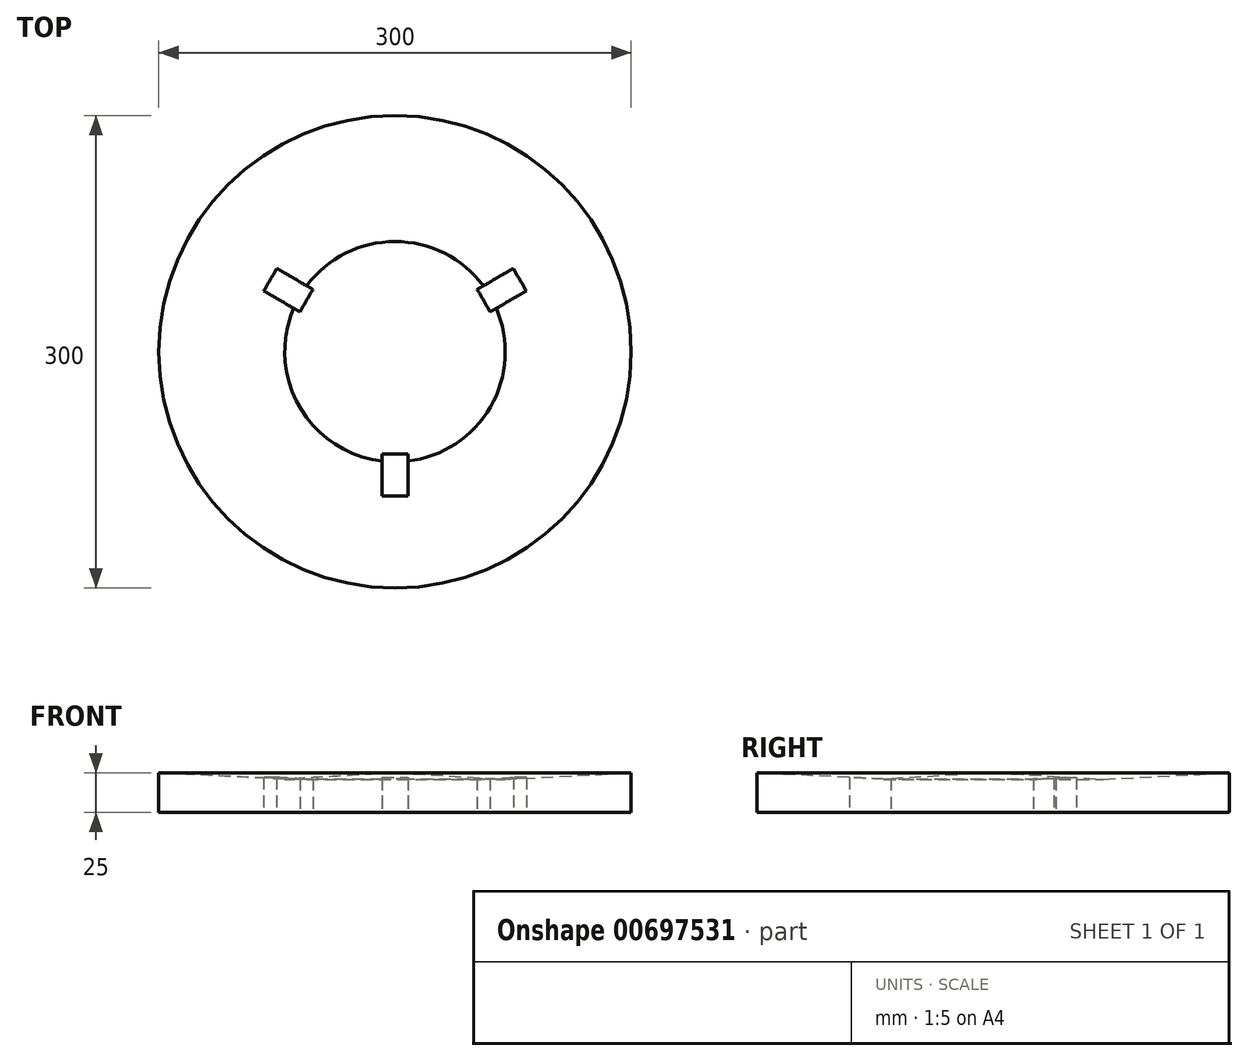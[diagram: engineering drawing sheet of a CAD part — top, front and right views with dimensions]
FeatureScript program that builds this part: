
annotation { "Feature Type Name" : "Feature", "Feature Type Description" : "" }
export const myFeature = defineFeature(function(context is Context, id is Id, definition is map)
    precondition{}
    {
        {
            var Q0;
            Q0=qCreatedBy(makeId("Front.planeOp"),FACE);
            var sketch = newSketch(context, id + "F0", { "sketchPlane" : qUnion([Q0])});
            skLineSegment(sketch, "E0", {"start": v(0, 0) * mm, "end": v(-150, 0) * mm});
            skLineSegment(sketch, "E1", {"start": v(-150, 0) * mm, "end": v(-150, 25) * mm});
            skLineSegment(sketch, "E2", {"start": v(0, 0) * mm, "end": v(0, 25) * mm});
            skLineSegment(sketch, "E3", {"start": v(0, 0) * mm, "end": v(-70, 0) * mm});
            skLineSegment(sketch, "E4", {"start": v(-70, 0) * mm, "end": v(-70, 21) * mm});
            skLineSegment(sketch, "E5", {"start": v(-70, 21) * mm, "end": v(-150, 25) * mm});
            skLineSegment(sketch, "E6", {"start": v(-70, 21) * mm, "end": v(0, 25) * mm});
            skSolve(sketch);
        }
        {
            var Q0;
            Q0=makeQuery(id+"F0.imprint","IMPRINT",FACE,{"disambiguationData":[TD([[makeQuery(id+"F0.imprint","IMPRINT",EDGE,{"derivedFrom":sQuery(id+"F0.wireOp",EDGE,"E0")}),-1.0]])]});
            var Q1;
            Q1=makeQuery(id+"F0.imprint","IMPRINT",FACE,{"disambiguationData":[TD([[makeQuery(id+"F0.imprint","IMPRINT",EDGE,{"derivedFrom":sQuery(id+"F0.wireOp",EDGE,"E2")}),1.0]])]});
            var Q2;
            Q2=sQuery(id+"F0.wireOp",EDGE,"E2");
            revolve(context, id + "F1", {"entities" : qUnion([Q0, Q1]), "axis" : qUnion([Q2]), "revolveType" : RevolveType.FULL});
        }
        {
            var Q0;
            Q0=makeQuery(id+"F1.opRevolve","SWEPT_FACE",FACE,{"disambiguationData":[OSD([sQuery(id+"F0.wireOp",EDGE,"E0"),sQuery(id+"F0.wireOp",EDGE,"E3")])]});
            var sketch = newSketch(context, id + "F2", { "sketchPlane" : qUnion([Q0])});
            skLineSegment(sketch, "E7.bottom", {"start": v(8.25, 91.5) * mm, "end": v(-8.25, 91.5) * mm});
            skLineSegment(sketch, "E7.top", {"start": v(8.25, 65) * mm, "end": v(-8.25, 65) * mm});
            skLineSegment(sketch, "E7.left", {"start": v(8.25, 91.5) * mm, "end": v(8.25, 65) * mm});
            skLineSegment(sketch, "E7.right", {"start": v(-8.25, 91.5) * mm, "end": v(-8.25, 65) * mm});
            skPoint(sketch, "E7.middle", {"position": v(0, 78.25) * mm});
            skLineSegment(sketch, "E8.1.0", {"start": v(-60.42, -25.36) * mm, "end": v(-52.17, -39.64) * mm});
            skLineSegment(sketch, "E8.1.1", {"start": v(-75.12, -52.9) * mm, "end": v(-52.17, -39.64) * mm});
            skLineSegment(sketch, "E8.1.2", {"start": v(-83.37, -38.6) * mm, "end": v(-60.42, -25.36) * mm});
            skLineSegment(sketch, "E8.1.3", {"start": v(-83.37, -38.6) * mm, "end": v(-75.12, -52.9) * mm});
            skLineSegment(sketch, "E8.2.0", {"start": v(52.17, -39.64) * mm, "end": v(60.42, -25.36) * mm});
            skLineSegment(sketch, "E8.2.1", {"start": v(83.37, -38.6) * mm, "end": v(60.42, -25.36) * mm});
            skLineSegment(sketch, "E8.2.2", {"start": v(75.12, -52.9) * mm, "end": v(52.17, -39.64) * mm});
            skLineSegment(sketch, "E8.2.3", {"start": v(75.12, -52.9) * mm, "end": v(83.37, -38.6) * mm});
            skPoint(sketch, "E8.center", {"position": v(0, 0) * mm});
            skSolve(sketch);
        }
        {
            var Q0;
            Q0 = qSketchRegion(id + "F2", true);
            extrude(context, id + "F3", {"entities" : qUnion([Q0]), "operationType" : NewBodyOperationType.REMOVE, "endBound" : BoundingType.UP_TO_NEXT, "oppositeDirection" : true, "depth" : 25 * mm, "offsetDistance" : 25 * mm});
        }
    });
